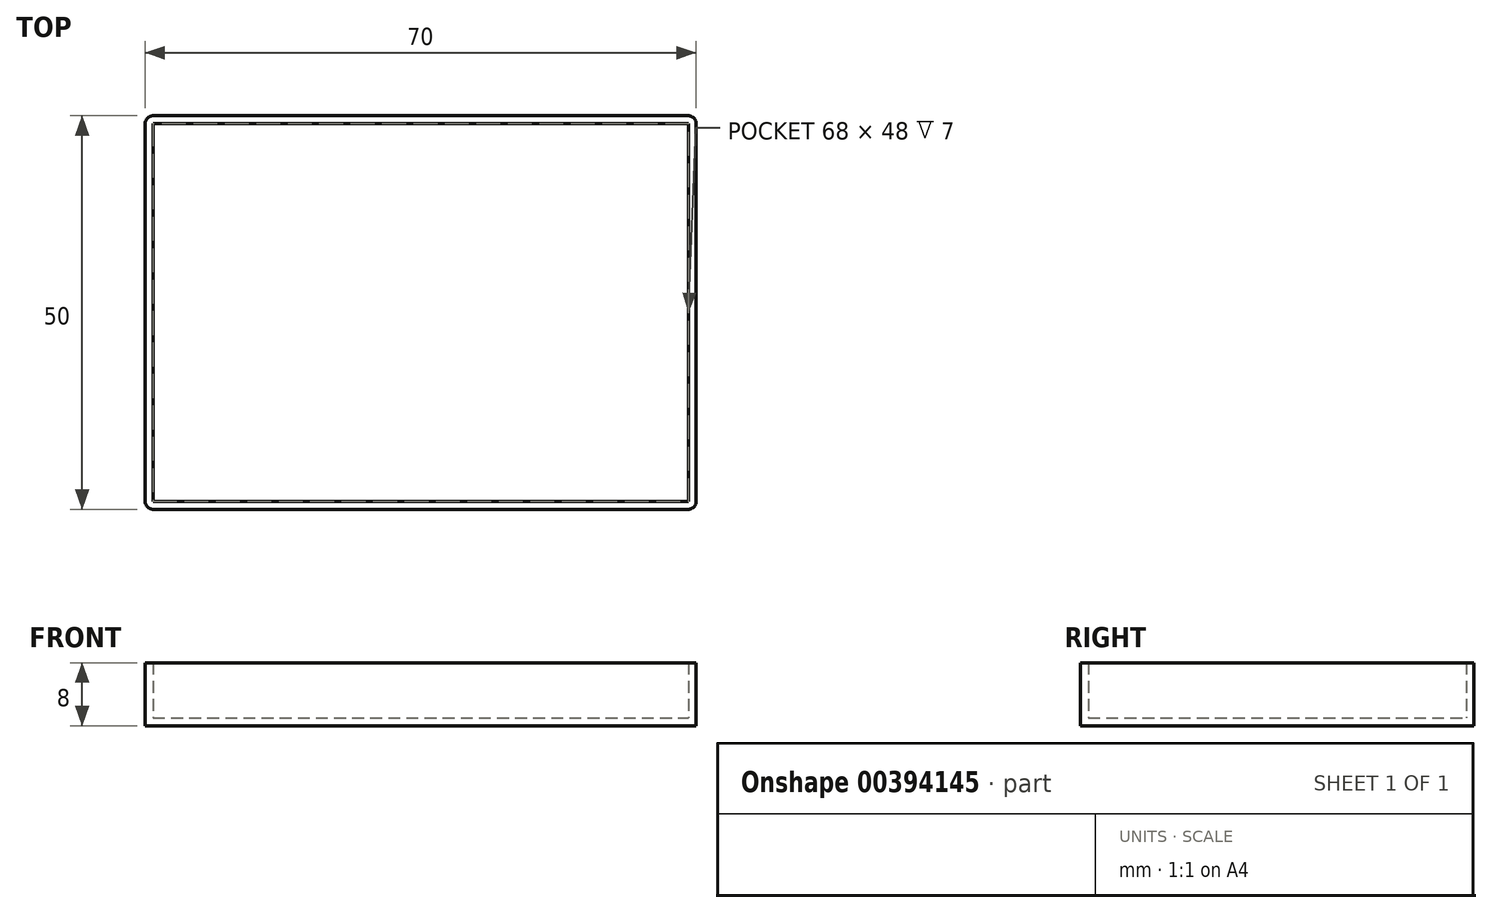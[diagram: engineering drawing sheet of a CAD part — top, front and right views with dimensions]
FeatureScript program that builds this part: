
annotation { "Feature Type Name" : "Feature", "Feature Type Description" : "" }
export const myFeature = defineFeature(function(context is Context, id is Id, definition is map)
    precondition{}
    {
        {
            var Q0;
            Q0=qCreatedBy(makeId("Top.planeOp"),FACE);
            var sketch = newSketch(context, id + "F0", { "sketchPlane" : qUnion([Q0])});
            skLineSegment(sketch, "E0.bottom", {"start": v(35, -25) * mm, "end": v(-35, -25) * mm});
            skLineSegment(sketch, "E0.top", {"start": v(35, 25) * mm, "end": v(-35, 25) * mm});
            skLineSegment(sketch, "E0.left", {"start": v(35, -25) * mm, "end": v(35, 25) * mm});
            skLineSegment(sketch, "E0.right", {"start": v(-35, -25) * mm, "end": v(-35, 25) * mm});
            skPoint(sketch, "E0.middle", {"position": v(0, 0) * mm});
            skSolve(sketch);
        }
        {
            var Q0;
            Q0=makeQuery(id+"F0.imprint","IMPRINT",FACE,{"disambiguationData":[TD([[makeQuery(id+"F0.imprint","IMPRINT",EDGE,{"derivedFrom":sQuery(id+"F0.wireOp",EDGE,"E0.bottom")}),-1.0]])]});
            extrude(context, id + "F1", {"entities" : qUnion([Q0]), "depth" : 1 * mm});
        }
        {
            var Q0;
            Q0=makeQuery(id+"F1.opExtrude","CAP_FACE",FACE,{"disambiguationData":[OSD([sQuery(id+"F0.wireOp",EDGE,"E0.bottom"),sQuery(id+"F0.wireOp",EDGE,"E0.top"),sQuery(id+"F0.wireOp",EDGE,"E0.left"),sQuery(id+"F0.wireOp",EDGE,"E0.right")])],"isStart":false});
            var sketch = newSketch(context, id + "F2", { "sketchPlane" : qUnion([Q0])});
            skLineSegment(sketch, "E1.0", {"start": v(34, -24) * mm, "end": v(34, 24) * mm});
            skLineSegment(sketch, "E1.1", {"start": v(-34, -24) * mm, "end": v(34, -24) * mm});
            skLineSegment(sketch, "E1.2", {"start": v(-34, 24) * mm, "end": v(-34, -24) * mm});
            skLineSegment(sketch, "E1.3", {"start": v(34, 24) * mm, "end": v(-34, 24) * mm});
            skLineSegment(sketch, "E2.0.0", {"start": v(35, -25) * mm, "end": v(35, 25) * mm});
            skLineSegment(sketch, "E2.0.1", {"start": v(35, 25) * mm, "end": v(-35, 25) * mm});
            skLineSegment(sketch, "E2.0.2", {"start": v(-35, 25) * mm, "end": v(-35, -25) * mm});
            skLineSegment(sketch, "E2.0.3", {"start": v(-35, -25) * mm, "end": v(35, -25) * mm});
            skSolve(sketch);
        }
        {
            var Q0;
            Q0=makeQuery(id+"F2.imprint","IMPRINT",FACE,{"disambiguationData":[TD([[makeQuery(id+"F2.imprint","IMPRINT",EDGE,{"derivedFrom":sQuery(id+"F2.wireOp",EDGE,"E1.0")}),-1.0]])]});
            extrude(context, id + "F3", {"entities" : qUnion([Q0]), "operationType" : NewBodyOperationType.ADD, "depth" : 7 * mm});
        }
        {
            var Q0;
            Q0=makeQuery(id+"F3.boolean.opBoolean","MERGE",EDGE,{"derivedFrom":[makeQuery(id+"F1.opExtrude","SWEPT_EDGE",EDGE,{"disambiguationData":[OSD([sQuery(id+"F0.wireOp",EDGE,"E0.bottom"),sQuery(id+"F0.wireOp",EDGE,"E0.right")])]}),makeQuery(id+"F3.opExtrude","SWEPT_EDGE",EDGE,{"disambiguationData":[OSD([sQuery(id+"F2.wireOp",EDGE,"E2.0.2"),sQuery(id+"F2.wireOp",EDGE,"E2.0.3")])]})]});
            var Q1;
            Q1=makeQuery(id+"F3.boolean.opBoolean","MERGE",EDGE,{"derivedFrom":[makeQuery(id+"F1.opExtrude","SWEPT_EDGE",EDGE,{"disambiguationData":[OSD([sQuery(id+"F0.wireOp",EDGE,"E0.bottom"),sQuery(id+"F0.wireOp",EDGE,"E0.left")])]}),makeQuery(id+"F3.opExtrude","SWEPT_EDGE",EDGE,{"disambiguationData":[OSD([sQuery(id+"F2.wireOp",EDGE,"E2.0.0"),sQuery(id+"F2.wireOp",EDGE,"E2.0.3")])]})]});
            var Q2;
            Q2=makeQuery(id+"F3.boolean.opBoolean","MERGE",EDGE,{"derivedFrom":[makeQuery(id+"F1.opExtrude","SWEPT_EDGE",EDGE,{"disambiguationData":[OSD([sQuery(id+"F0.wireOp",EDGE,"E0.top"),sQuery(id+"F0.wireOp",EDGE,"E0.left")])]}),makeQuery(id+"F3.opExtrude","SWEPT_EDGE",EDGE,{"disambiguationData":[OSD([sQuery(id+"F2.wireOp",EDGE,"E2.0.0"),sQuery(id+"F2.wireOp",EDGE,"E2.0.1")])]})]});
            var Q3;
            Q3=makeQuery(id+"F3.boolean.opBoolean","MERGE",EDGE,{"derivedFrom":[makeQuery(id+"F1.opExtrude","SWEPT_EDGE",EDGE,{"disambiguationData":[OSD([sQuery(id+"F0.wireOp",EDGE,"E0.top"),sQuery(id+"F0.wireOp",EDGE,"E0.right")])]}),makeQuery(id+"F3.opExtrude","SWEPT_EDGE",EDGE,{"disambiguationData":[OSD([sQuery(id+"F2.wireOp",EDGE,"E2.0.1"),sQuery(id+"F2.wireOp",EDGE,"E2.0.2")])]})]});
            fillet(context, id + "F4", {"entities" : qUnion([Q0, Q1, Q2, Q3]), "radius" : 1 * mm, "tangentPropagation" : true, "allowEdgeOverflow" : false});
        }
    });
